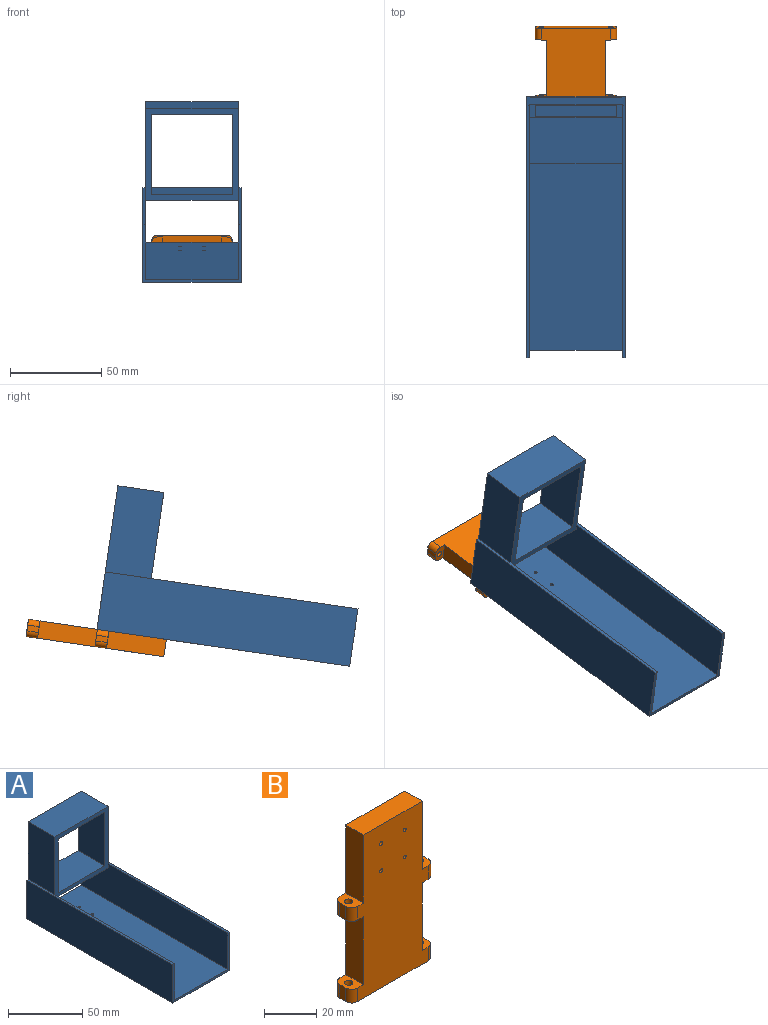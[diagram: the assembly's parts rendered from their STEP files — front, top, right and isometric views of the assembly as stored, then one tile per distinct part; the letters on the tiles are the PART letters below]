
ASSEMBLY  parts=2 mates=1
PART A: 23 faces, bbox 54x139.7x79.4 mm
  f0: plane 139.7x30.16mm, normal (-1,0,0), area 4133.1mm2, adj f1,f2,f8,f9,f15,f18
  f1: plane 139.7x1.59mm, normal (0,0,1), area 221.8mm2, adj f0,f7,f8,f9,f10
  f2: plane 139.7x50.8mm, normal (0,0,1), area 7088.8mm2, adj f0,f3,f8,f9,f19,f20,f21,f22
  f3: plane 139.7x30.16mm, normal (1,0,0), area 4133.1mm2, adj f2,f4,f8,f9,f15,f18
  f4: plane 139.7x1.59mm, normal (0,0,1), area 221.8mm2, adj f3,f5,f8,f9,f11
  f5: plane 139.7x31.75mm, normal (-1,0,0), area 4435.5mm2, adj f4,f6,f8,f9
  f6: plane 139.7x53.98mm, normal (0,0,-1), area 7532.4mm2, adj f5,f7,f8,f9,f19,f20,f21,f22
  f7: plane 139.7x31.75mm, normal (1,0,0), area 4435.5mm2, adj f1,f6,f8,f9
  f8: plane 53.98x31.75mm, normal (0,-1,0), area 181.5mm2, adj f0,f1,f2,f3,f4,f5,f6,f7
  f9: plane 79.38x53.98mm, normal (0,1,0), area 786.3mm2, adj f0,f1,f2,f3,f4,f5,f6,f7
  f10: plane 47.63x25.4mm, normal (1,0,0), area 1209.7mm2, adj f1,f9,f16,f18
  f11: plane 47.63x25.4mm, normal (-1,0,0), area 1209.7mm2, adj f4,f9,f16,f18
  f12: plane 44.45x25.4mm, normal (-1,0,0), area 1129mm2, adj f9,f13,f17,f18
  f13: plane 44.45x25.4mm, normal (0,0,1), area 1129mm2, adj f9,f12,f14,f18
  f14: plane 44.45x25.4mm, normal (1,0,0), area 1129mm2, adj f9,f13,f17,f18
  f15: plane 50.8x25.4mm, normal (0,0,-1), area 1290.3mm2, adj f0,f3,f9,f18
  f16: plane 50.8x25.4mm, normal (0,0,1), area 1290.3mm2, adj f9,f10,f11,f18
  f17: plane 44.45x25.4mm, normal (0,0,-1), area 1129mm2, adj f9,f12,f14,f18
  f18: plane 50.8x50.8mm, normal (0,-1,0), area 604.8mm2, adj f0,f3,f10,f11,f12,f13,f14,f15
  f19: cylinder r=0.79mm len=1.59mm, axis (0,0,-1), area 7.9mm2, adj f2,f6
  f20: cylinder r=0.79mm len=1.59mm, axis (0,0,-1), area 7.9mm2, adj f2,f6
  f21: cylinder r=0.79mm len=1.59mm, axis (0,0,-1), area 7.9mm2, adj f2,f6
  f22: cylinder r=0.79mm len=1.59mm, axis (0,0,-1), area 7.9mm2, adj f2,f6
PART B: 34 faces, bbox 44.5x9.5x76.2 mm
  f0: plane 9.53x6.35mm, normal (0,0,1), area 48.2mm2, adj f1,f19,f20,f21,f25,f32,f33
  f1: plane 6.35x3.18mm, normal (-1,0,0), area 20.2mm2, adj f0,f2,f32,f33
  f2: plane 9.53x6.35mm, normal (0,0,-1), area 48.2mm2, adj f1,f3,f20,f21,f25,f32,f33
  f3: plane 31.75x9.53mm, normal (-1,0,0), area 302.4mm2, adj f2,f4,f20,f21
  f4: plane 9.53x6.35mm, normal (0,0,1), area 48.2mm2, adj f3,f5,f20,f21,f24,f29,f31
  f5: plane 6.35x3.18mm, normal (-1,0,0), area 20.2mm2, adj f4,f6,f29,f31
  f6: plane 44.45x9.53mm, normal (0,0,-1), area 398.9mm2, adj f5,f7,f20,f21,f23,f24,f26,f28
  f7: plane 6.35x3.18mm, normal (1,0,0), area 20.2mm2, adj f6,f8,f26,f28
  f8: plane 9.53x6.35mm, normal (0,0,1), area 48.2mm2, adj f7,f9,f20,f21,f23,f26,f28
  f9: plane 31.75x9.53mm, normal (1,0,0), area 302.4mm2, adj f8,f10,f20,f21
  f10: plane 9.53x6.35mm, normal (0,0,-1), area 48.2mm2, adj f9,f11,f20,f21,f22,f27,f30
  f11: plane 6.35x3.18mm, normal (1,0,0), area 20.2mm2, adj f10,f12,f27,f30
  f12: plane 9.53x6.35mm, normal (0,0,1), area 48.2mm2, adj f11,f13,f20,f21,f22,f27,f30
  f13: plane 31.75x9.53mm, normal (1,0,0), area 302.4mm2, adj f12,f14,f20,f21
  f14: plane 31.75x9.53mm, normal (0,0,1), area 302.4mm2, adj f13,f19,f20,f21
  f15: cylinder r=0.79mm len=9.53mm, axis (0,1,0), area 47.5mm2, adj f20,f21
  f16: cylinder r=0.79mm len=9.53mm, axis (0,1,0), area 47.5mm2, adj f20,f21
  f17: cylinder r=0.79mm len=9.53mm, axis (0,1,0), area 47.5mm2, adj f20,f21
  f18: cylinder r=0.79mm len=9.53mm, axis (0,1,0), area 47.5mm2, adj f20,f21
  f19: plane 31.75x9.53mm, normal (-1,0,0), area 302.4mm2, adj f0,f14,f20,f21
  f20: plane 76.2x38.1mm, normal (0,-1,0), area 2492.1mm2, adj f0,f2,f3,f4,f6,f8,f9,f10
  f21: plane 76.2x38.1mm, normal (0,1,0), area 2492.1mm2, adj f0,f2,f3,f4,f6,f8,f9,f10
  f22: cylinder r=1.59mm len=6.35mm, axis (0,0,-1), area 63.3mm2, adj f10,f12
  f23: cylinder r=1.59mm len=6.35mm, axis (0,0,-1), area 63.3mm2, adj f6,f8
  f24: cylinder r=1.59mm len=6.35mm, axis (0,0,-1), area 63.3mm2, adj f4,f6
  f25: cylinder r=1.59mm len=6.35mm, axis (0,0,-1), area 63.3mm2, adj f0,f2
  f26: cylinder r=3.17mm len=6.35mm, axis (0,0,1), area 31.7mm2, adj f6,f7,f8,f21
  f27: cylinder r=3.17mm len=6.35mm, axis (0,0,1), area 31.7mm2, adj f10,f11,f12,f21
  f28: cylinder r=3.17mm len=6.35mm, axis (0,0,-1), area 31.7mm2, adj f6,f7,f8,f20
  f29: cylinder r=3.17mm len=6.35mm, axis (0,0,1), area 31.7mm2, adj f4,f5,f6,f20
  f30: cylinder r=3.17mm len=6.35mm, axis (0,0,-1), area 31.7mm2, adj f10,f11,f12,f20
  f31: cylinder r=3.17mm len=6.35mm, axis (0,0,-1), area 31.7mm2, adj f4,f5,f6,f21
  f32: cylinder r=3.17mm len=6.35mm, axis (0,0,-1), area 31.7mm2, adj f0,f1,f2,f21
  f33: cylinder r=3.17mm len=6.35mm, axis (0,0,1), area 31.7mm2, adj f0,f1,f2,f20
PLACE A rot(axis=(1,0,0),8.3deg) t=(-167.5,-2.69,116.87)mm
PLACE B rot(axis=(1,0,0),98.3deg) t=(0,21.99,47.4)mm
MATE fastened A.f21 <-> B.f15  axis (0,0.14,-0.99) through (-28.94,-21.63,41.03)mm
